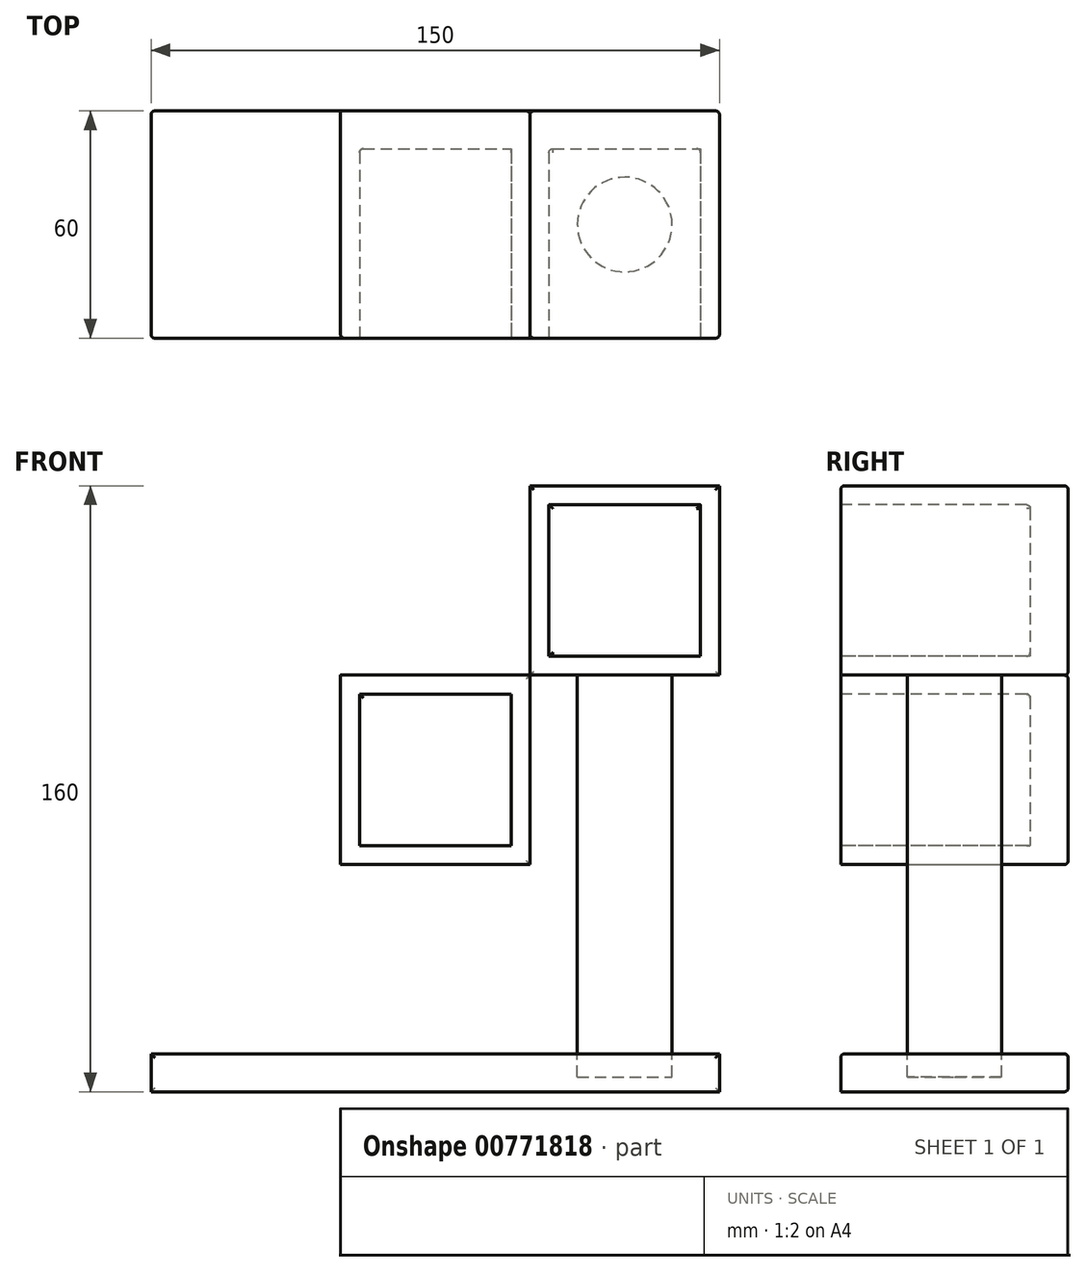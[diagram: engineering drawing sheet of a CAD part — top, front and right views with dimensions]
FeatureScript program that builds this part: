
annotation { "Feature Type Name" : "Feature", "Feature Type Description" : "" }
export const myFeature = defineFeature(function(context is Context, id is Id, definition is map)
    precondition{}
    {
        {
            var Q0;
            Q0=qCreatedBy(makeId("Front.planeOp"),FACE);
            var sketch = newSketch(context, id + "F0", { "sketchPlane" : qUnion([Q0])});
            skLineSegment(sketch, "E0.bottom", {"start": v(-61.34, 16.9) * mm, "end": v(88.66, 16.9) * mm});
            skLineSegment(sketch, "E0.top", {"start": v(-61.34, 6.9) * mm, "end": v(88.66, 6.9) * mm});
            skLineSegment(sketch, "E0.left", {"start": v(-61.34, 16.9) * mm, "end": v(-61.34, 6.9) * mm});
            skLineSegment(sketch, "E0.right", {"start": v(88.66, 16.9) * mm, "end": v(88.66, 6.9) * mm});
            skLineSegment(sketch, "E1.bottom", {"start": v(-61.34, 16.9) * mm, "end": v(-11.34, 16.9) * mm});
            skLineSegment(sketch, "E1.top", {"start": v(-61.34, 66.9) * mm, "end": v(-11.34, 66.9) * mm});
            skLineSegment(sketch, "E1.left", {"start": v(-61.34, 16.9) * mm, "end": v(-61.34, 66.9) * mm});
            skLineSegment(sketch, "E1.right", {"start": v(-11.34, 16.9) * mm, "end": v(-11.34, 66.9) * mm});
            skLineSegment(sketch, "E2.bottom", {"start": v(-11.34, 66.9) * mm, "end": v(38.66, 66.9) * mm});
            skLineSegment(sketch, "E2.top", {"start": v(-11.34, 116.9) * mm, "end": v(38.66, 116.9) * mm});
            skLineSegment(sketch, "E2.left", {"start": v(-11.34, 66.9) * mm, "end": v(-11.34, 116.9) * mm});
            skLineSegment(sketch, "E2.right", {"start": v(38.66, 66.9) * mm, "end": v(38.66, 116.9) * mm});
            skLineSegment(sketch, "E3.bottom", {"start": v(38.66, 116.9) * mm, "end": v(88.66, 116.9) * mm});
            skLineSegment(sketch, "E3.top", {"start": v(38.66, 166.9) * mm, "end": v(88.66, 166.9) * mm});
            skLineSegment(sketch, "E3.left", {"start": v(38.66, 116.9) * mm, "end": v(38.66, 166.9) * mm});
            skLineSegment(sketch, "E3.right", {"start": v(88.66, 116.9) * mm, "end": v(88.66, 166.9) * mm});
            skLineSegment(sketch, "E4.left", {"start": v(38.66, 148.79) * mm, "end": v(38.66, 140.1) * mm});
            skLineSegment(sketch, "E4.right", {"start": v(88.66, 148.79) * mm, "end": v(88.66, 140.1) * mm});
            skLineSegment(sketch, "E5.bottom", {"start": v(88.66, 116.9) * mm, "end": v(73.66, 116.9) * mm});
            skLineSegment(sketch, "E5.top", {"start": v(88.66, 16.9) * mm, "end": v(73.66, 16.9) * mm});
            skSolve(sketch);
        }
        {
            var Q0;
            Q0=makeQuery(id+"F0.imprint","IMPRINT",FACE,{"disambiguationData":[TD([[makeQuery(id+"F0.imprint","IMPRINT",EDGE,{"derivedFrom":sQuery(id+"F0.wireOp",EDGE,"E2.bottom")}),1.0]])]});
            var sketch = newSketch(context, id + "F1", { "sketchPlane" : qUnion([Q0])});
            skSolve(sketch);
        }
        {
            var Q0;
            {var subQ3=sQuery(id+"F0.wireOp",EDGE,"E3.bottom");Q0=makeQuery(id+"F0.imprint","IMPRINT",FACE,{"disambiguationData":[TD([[makeQuery(id+"F0.imprint","IMPRINT",EDGE,{"derivedFrom":subQ3}),1.0]])]});}
            var Q1;
            Q1=makeQuery(id+"F0.imprint","IMPRINT",FACE,{"disambiguationData":[TD([[makeQuery(id+"F0.imprint","IMPRINT",EDGE,{"derivedFrom":sQuery(id+"F0.wireOp",EDGE,"E1.bottom")}),1.0]])]});
            var Q2;
            Q2=makeQuery(id+"F0.imprint","IMPRINT",FACE,{"disambiguationData":[TD([[makeQuery(id+"F0.imprint","IMPRINT",EDGE,{"derivedFrom":sQuery(id+"F0.wireOp",EDGE,"E5.bottom")}),1.0]])]});
            var Q3;
            Q3=makeQuery(id+"F0.imprint","IMPRINT",FACE,{"disambiguationData":[TD([[makeQuery(id+"F0.imprint","IMPRINT",EDGE,{"derivedFrom":sQuery(id+"F0.wireOp",EDGE,"E0.bottom")}),-1.0]])]});
            var Q4;
            Q4=makeQuery(id+"F1.imprint","IMPRINT",FACE,{"disambiguationData":[TD([[makeQuery(id+"F1.imprint","IMPRINT",EDGE,{"derivedFrom":makeQuery(id+"F0.imprint","IMPRINT",EDGE,{"derivedFrom":sQuery(id+"F0.wireOp",EDGE,"E2.bottom")})}),1.0]])]});
            extrude(context, id + "F2", {"entities" : qUnion([Q0, Q1, Q2, Q3, Q4]), "depth" : 60 * mm, "offsetDistance" : 25 * mm});
        }
        {
            var Q0;
            Q0=makeQuery(id+"F2.opExtrude","CAP_FACE",FACE,{"disambiguationData":[OSD([sQuery(id+"F0.wireOp",EDGE,"E0.bottom"),sQuery(id+"F0.wireOp",EDGE,"E0.top"),sQuery(id+"F0.wireOp",EDGE,"E0.left"),sQuery(id+"F0.wireOp",EDGE,"E0.right"),sQuery(id+"F0.wireOp",EDGE,"E1.top"),sQuery(id+"F0.wireOp",EDGE,"E1.left"),sQuery(id+"F0.wireOp",EDGE,"E1.right"),sQuery(id+"F0.wireOp",EDGE,"E3.bottom"),sQuery(id+"F0.wireOp",EDGE,"E3.top"),sQuery(id+"F0.wireOp",EDGE,"E3.left"),sQuery(id+"F0.wireOp",EDGE,"E3.right"),sQuery(id+"F0.wireOp",EDGE,"E4.left"),sQuery(id+"F0.wireOp",EDGE,"E4.right"),sQuery(id+"F0.wireOp",EDGE,"E5.left"),sQuery(id+"F0.wireOp",EDGE,"E5.right")])],"isStart":false});
            var sketch = newSketch(context, id + "F3", { "sketchPlane" : qUnion([Q0])});
            skLineSegment(sketch, "E6.bottom", {"start": v(-56.34, 61.9) * mm, "end": v(-16.34, 61.9) * mm});
            skLineSegment(sketch, "E6.top", {"start": v(-56.34, 16.9) * mm, "end": v(-16.34, 16.9) * mm});
            skLineSegment(sketch, "E6.left", {"start": v(-56.34, 61.9) * mm, "end": v(-56.34, 16.9) * mm});
            skLineSegment(sketch, "E6.right", {"start": v(-16.34, 61.9) * mm, "end": v(-16.34, 16.9) * mm});
            skLineSegment(sketch, "E7.bottom", {"start": v(43.66, 161.9) * mm, "end": v(83.66, 161.9) * mm});
            skLineSegment(sketch, "E7.top", {"start": v(43.66, 121.9) * mm, "end": v(83.66, 121.9) * mm});
            skLineSegment(sketch, "E7.left", {"start": v(43.66, 161.9) * mm, "end": v(43.66, 121.9) * mm});
            skLineSegment(sketch, "E7.right", {"start": v(83.66, 161.9) * mm, "end": v(83.66, 121.9) * mm});
            skSolve(sketch);
        }
        {
            var Q0;
            Q0=makeQuery(id+"F3.imprint","IMPRINT",FACE,{"disambiguationData":[TD([[makeQuery(id+"F3.imprint","IMPRINT",EDGE,{"derivedFrom":sQuery(id+"F3.wireOp",EDGE,"E6.bottom")}),-1.0]])]});
            var Q1;
            Q1=makeQuery(id+"F3.imprint","IMPRINT",FACE,{"disambiguationData":[TD([[makeQuery(id+"F3.imprint","IMPRINT",EDGE,{"derivedFrom":sQuery(id+"F3.wireOp",EDGE,"E7.bottom")}),-1.0]])]});
            extrude(context, id + "F4", {"entities" : qUnion([Q0, Q1]), "operationType" : NewBodyOperationType.REMOVE, "oppositeDirection" : true, "depth" : 50 * mm, "offsetDistance" : 25 * mm});
        }
        {
            var Q0;
            Q0=makeQuery(id+"F2.opExtrude","CAP_FACE",FACE,{"disambiguationData":[OSD([sQuery(id+"F0.wireOp",EDGE,"E2.bottom"),sQuery(id+"F0.wireOp",EDGE,"E2.top"),sQuery(id+"F0.wireOp",EDGE,"E2.left"),sQuery(id+"F0.wireOp",EDGE,"E2.right")])],"isStart":false});
            var sketch = newSketch(context, id + "F5", { "sketchPlane" : qUnion([Q0])});
            skLineSegment(sketch, "E8.bottom", {"start": v(-6.34, 111.9) * mm, "end": v(33.66, 111.9) * mm});
            skLineSegment(sketch, "E8.top", {"start": v(-6.34, 71.9) * mm, "end": v(33.66, 71.9) * mm});
            skLineSegment(sketch, "E8.left", {"start": v(-6.34, 111.9) * mm, "end": v(-6.34, 71.9) * mm});
            skLineSegment(sketch, "E8.right", {"start": v(33.66, 111.9) * mm, "end": v(33.66, 71.9) * mm});
            skSolve(sketch);
        }
        {
            var Q0;
            Q0 = qSketchRegion(id + "F5", true);
            extrude(context, id + "F6", {"entities" : qUnion([Q0]), "operationType" : NewBodyOperationType.REMOVE, "oppositeDirection" : true, "depth" : 50 * mm, "offsetDistance" : 25 * mm});
        }
        {
            var Q0;
            Q0=makeQuery(id+"F2.opExtrude","CAP_EDGE",EDGE,{"disambiguationData":[OSD([sQuery(id+"F0.wireOp",EDGE,"E1.right")])],"isStart":false});
            var Q1;
            Q1=makeQuery(id+"F2.opExtrude","CAP_EDGE",EDGE,{"disambiguationData":[OSD([sQuery(id+"F0.wireOp",EDGE,"E1.top")])],"isStart":false});
            var Q2;
            Q2=makeQuery(id+"F2.opExtrude","CAP_EDGE",EDGE,{"disambiguationData":[OSD([sQuery(id+"F0.wireOp",EDGE,"E0.left"),sQuery(id+"F0.wireOp",EDGE,"E1.left")])],"isStart":false});
            var Q3;
            Q3=makeQuery(id+"F2.opExtrude","CAP_EDGE",EDGE,{"disambiguationData":[OSD([sQuery(id+"F0.wireOp",EDGE,"E0.bottom")])],"isStart":false});
            var Q4;
            Q4=makeQuery(id+"F2.opExtrude","CAP_EDGE",EDGE,{"disambiguationData":[OSD([sQuery(id+"F0.wireOp",EDGE,"E0.right"),sQuery(id+"F0.wireOp",EDGE,"E3.right"),sQuery(id+"F0.wireOp",EDGE,"E4.right"),sQuery(id+"F0.wireOp",EDGE,"E5.left")])],"isStart":true});
            var Q5;
            Q5=makeQuery(id+"F2.opExtrude","CAP_EDGE",EDGE,{"disambiguationData":[OSD([sQuery(id+"F0.wireOp",EDGE,"E0.right"),sQuery(id+"F0.wireOp",EDGE,"E3.right"),sQuery(id+"F0.wireOp",EDGE,"E4.right"),sQuery(id+"F0.wireOp",EDGE,"E5.left")])],"isStart":false});
            var Q6;
            Q6=makeQuery(id+"F4.boolean.opBoolean","COPY",FACE,{"derivedFrom":makeQuery(id+"F4.opExtrude","CAP_FACE",FACE,{"disambiguationData":[OSD([sQuery(id+"F3.wireOp",EDGE,"E6.bottom"),sQuery(id+"F3.wireOp",EDGE,"E6.top"),sQuery(id+"F3.wireOp",EDGE,"E6.left"),sQuery(id+"F3.wireOp",EDGE,"E6.right")])],"isStart":false})});
            var Q7;
            Q7=makeQuery(id+"F6.boolean.opBoolean","COPY",EDGE,{"derivedFrom":makeQuery(id+"F6.opExtrude","CAP_EDGE",EDGE,{"disambiguationData":[OSD([sQuery(id+"F5.wireOp",EDGE,"E8.left")])],"isStart":false})});
            var Q8;
            Q8=makeQuery(id+"F6.boolean.opBoolean","COPY",EDGE,{"derivedFrom":makeQuery(id+"F6.opExtrude","CAP_EDGE",EDGE,{"disambiguationData":[OSD([sQuery(id+"F5.wireOp",EDGE,"E8.bottom")])],"isStart":false})});
            var Q9;
            Q9=makeQuery(id+"F6.boolean.opBoolean","COPY",EDGE,{"derivedFrom":makeQuery(id+"F6.opExtrude","CAP_EDGE",EDGE,{"disambiguationData":[OSD([sQuery(id+"F5.wireOp",EDGE,"E8.top")])],"isStart":true})});
            var Q10;
            Q10=makeQuery(id+"F6.boolean.opBoolean","COPY",EDGE,{"derivedFrom":makeQuery(id+"F6.opExtrude","CAP_EDGE",EDGE,{"disambiguationData":[OSD([sQuery(id+"F5.wireOp",EDGE,"E8.right")])],"isStart":true})});
            var Q11;
            Q11=makeQuery(id+"F2.opExtrude","CAP_EDGE",EDGE,{"disambiguationData":[OSD([sQuery(id+"F0.wireOp",EDGE,"E3.left"),sQuery(id+"F0.wireOp",EDGE,"E4.left")])],"isStart":false});
            var Q12;
            Q12=makeQuery(id+"F2.opExtrude","CAP_EDGE",EDGE,{"disambiguationData":[OSD([sQuery(id+"F0.wireOp",EDGE,"E3.top")])],"isStart":false});
            var Q13;
            Q13=makeQuery(id+"F4.boolean.opBoolean","COPY",FACE,{"derivedFrom":makeQuery(id+"F4.opExtrude","CAP_FACE",FACE,{"disambiguationData":[OSD([sQuery(id+"F3.wireOp",EDGE,"E7.bottom"),sQuery(id+"F3.wireOp",EDGE,"E7.top"),sQuery(id+"F3.wireOp",EDGE,"E7.left"),sQuery(id+"F3.wireOp",EDGE,"E7.right")])],"isStart":false})});
            var Q14;
            Q14=makeQuery(id+"F2.opExtrude","CAP_EDGE",EDGE,{"disambiguationData":[OSD([sQuery(id+"F0.wireOp",EDGE,"E1.right")])],"isStart":true});
            var Q15;
            Q15=makeQuery(id+"F2.opExtrude","CAP_EDGE",EDGE,{"disambiguationData":[OSD([sQuery(id+"F0.wireOp",EDGE,"E1.top")])],"isStart":true});
            var Q16;
            Q16=makeQuery(id+"F2.opExtrude","CAP_EDGE",EDGE,{"disambiguationData":[OSD([sQuery(id+"F0.wireOp",EDGE,"E0.left"),sQuery(id+"F0.wireOp",EDGE,"E1.left")])],"isStart":true});
            var Q17;
            Q17=makeQuery(id+"F2.opExtrude","CAP_EDGE",EDGE,{"disambiguationData":[OSD([sQuery(id+"F0.wireOp",EDGE,"E0.bottom")])],"isStart":true});
            var Q18;
            Q18=makeQuery(id+"F2.opExtrude","CAP_EDGE",EDGE,{"disambiguationData":[OSD([sQuery(id+"F0.wireOp",EDGE,"E2.bottom")])],"isStart":true});
            var Q19;
            Q19=makeQuery(id+"F2.opExtrude","CAP_EDGE",EDGE,{"disambiguationData":[OSD([sQuery(id+"F0.wireOp",EDGE,"E2.right")])],"isStart":true});
            var Q20;
            Q20=makeQuery(id+"F2.opExtrude","CAP_EDGE",EDGE,{"disambiguationData":[OSD([sQuery(id+"F0.wireOp",EDGE,"E2.left")])],"isStart":false});
            var Q21;
            Q21=makeQuery(id+"F2.opExtrude","CAP_EDGE",EDGE,{"disambiguationData":[OSD([sQuery(id+"F0.wireOp",EDGE,"E2.top")])],"isStart":true});
            var Q22;
            Q22=makeQuery(id+"F2.opExtrude","CAP_EDGE",EDGE,{"disambiguationData":[OSD([sQuery(id+"F0.wireOp",EDGE,"E3.left"),sQuery(id+"F0.wireOp",EDGE,"E4.left")])],"isStart":true});
            var Q23;
            Q23=makeQuery(id+"F2.opExtrude","CAP_EDGE",EDGE,{"disambiguationData":[OSD([sQuery(id+"F0.wireOp",EDGE,"E3.top")])],"isStart":true});
            var Q24;
            Q24=makeQuery(id+"F2.opExtrude","CAP_FACE",FACE,{"disambiguationData":[OSD([sQuery(id+"F0.wireOp",EDGE,"E0.bottom"),sQuery(id+"F0.wireOp",EDGE,"E0.top"),sQuery(id+"F0.wireOp",EDGE,"E0.left"),sQuery(id+"F0.wireOp",EDGE,"E0.right"),sQuery(id+"F0.wireOp",EDGE,"E1.top"),sQuery(id+"F0.wireOp",EDGE,"E1.left"),sQuery(id+"F0.wireOp",EDGE,"E1.right"),sQuery(id+"F0.wireOp",EDGE,"E3.bottom"),sQuery(id+"F0.wireOp",EDGE,"E3.top"),sQuery(id+"F0.wireOp",EDGE,"E3.left"),sQuery(id+"F0.wireOp",EDGE,"E3.right"),sQuery(id+"F0.wireOp",EDGE,"E4.left"),sQuery(id+"F0.wireOp",EDGE,"E4.right"),sQuery(id+"F0.wireOp",EDGE,"E5.left"),sQuery(id+"F0.wireOp",EDGE,"E5.right")])],"isStart":true});
            fillet(context, id + "F7", {"entities" : qUnion([Q0, Q1, Q2, Q3, Q4, Q5, Q6, Q7, Q8, Q9, Q10, Q11, Q12, Q13, Q14, Q15, Q16, Q17, Q18, Q19, Q20, Q21, Q22, Q23, Q24]), "radius" : 1 * mm, "tangentPropagation" : true, "allowEdgeOverflow" : false});
        }
        {
            var Q0;
            Q0=makeQuery(id+"F2.opExtrude","SWEPT_FACE",FACE,{"disambiguationData":[OSD([sQuery(id+"F0.wireOp",EDGE,"E3.bottom"),sQuery(id+"F0.wireOp",EDGE,"E5.bottom")])]});
            var sketch = newSketch(context, id + "F8", { "sketchPlane" : qUnion([Q0])});
            skCircle(sketch, "E9", {"center": v(63.66, 30) * mm, "radius": 12.5 * mm});
            skPoint(sketch, "E10.start.orphan", {"position": v(88.66, 30) * mm});
            skPoint(sketch, "E11.trimOffspring.end.orphan", {"position": v(63.66, 0) * mm});
            skPoint(sketch, "E12.trimOffspring.end.orphan", {"position": v(38.66, 30) * mm});
            skPoint(sketch, "E13.start.orphan", {"position": v(63.66, 60) * mm});
            skSolve(sketch);
        }
        {
            var Q0;
            Q0 = qSketchRegion(id + "F8", true);
            extrude(context, id + "F9", {"entities" : qUnion([Q0]), "depth" : 106.1 * mm, "offsetDistance" : 25 * mm});
        }
        {
            var Q0;
            Q0=makeQuery(id+"F2.opExtrude","CAP_FACE",FACE,{"disambiguationData":[OSD([sQuery(id+"F0.wireOp",EDGE,"E3.bottom"),sQuery(id+"F0.wireOp",EDGE,"E3.top"),sQuery(id+"F0.wireOp",EDGE,"E3.left"),sQuery(id+"F0.wireOp",EDGE,"E3.right"),sQuery(id+"F0.wireOp",EDGE,"E4.left"),sQuery(id+"F0.wireOp",EDGE,"E4.right"),sQuery(id+"F0.wireOp",EDGE,"E5.bottom")])],"isStart":false});
            var sketch = newSketch(context, id + "F10", { "sketchPlane" : qUnion([Q0])});
            skLineSegment(sketch, "E14.bottom", {"start": v(44.66, 160.9) * mm, "end": v(83.66, 160.9) * mm});
            skLineSegment(sketch, "E14.top", {"start": v(44.66, 121.9) * mm, "end": v(83.66, 121.9) * mm});
            skLineSegment(sketch, "E14.left", {"start": v(44.66, 160.9) * mm, "end": v(44.66, 121.9) * mm});
            skLineSegment(sketch, "E14.right", {"start": v(83.66, 160.9) * mm, "end": v(83.66, 121.9) * mm});
            skSolve(sketch);
        }
        {
            var Q0;
            Q0 = qSketchRegion(id + "F10", true);
            extrude(context, id + "F11", {"entities" : qUnion([Q0]), "operationType" : NewBodyOperationType.REMOVE, "oppositeDirection" : true, "depth" : 50 * mm, "offsetDistance" : 25 * mm});
        }
    });
